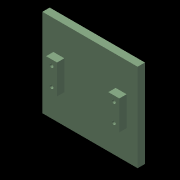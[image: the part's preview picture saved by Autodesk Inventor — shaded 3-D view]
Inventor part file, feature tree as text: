
AUTODESK INVENTOR PART (.ipt)
format: ipt  version: 2020 (Build 240168000, 168)  size: 137,728 bytes
history: native  units: mm
features: extrude x4, other x1, projected_geometry x1
ambient origin geometry x8: Origin, YZ Plane, XZ Plane, XY Plane, X Axis, Y Axis, Z Axis, Center Point
bodies: Body1 (feature_tree)
feature tree (6):
  other  "實體1"
  extrude  "Extrusion1"  Depth=10.0mm
  extrude  "Extrusion2"  Depth=3.0mm
  extrude  "Extrusion3"  Depth=2.0mm
  extrude  "Extrusion4"  Depth=2.0mm
  projected_geometry  "Projected Loop1"
